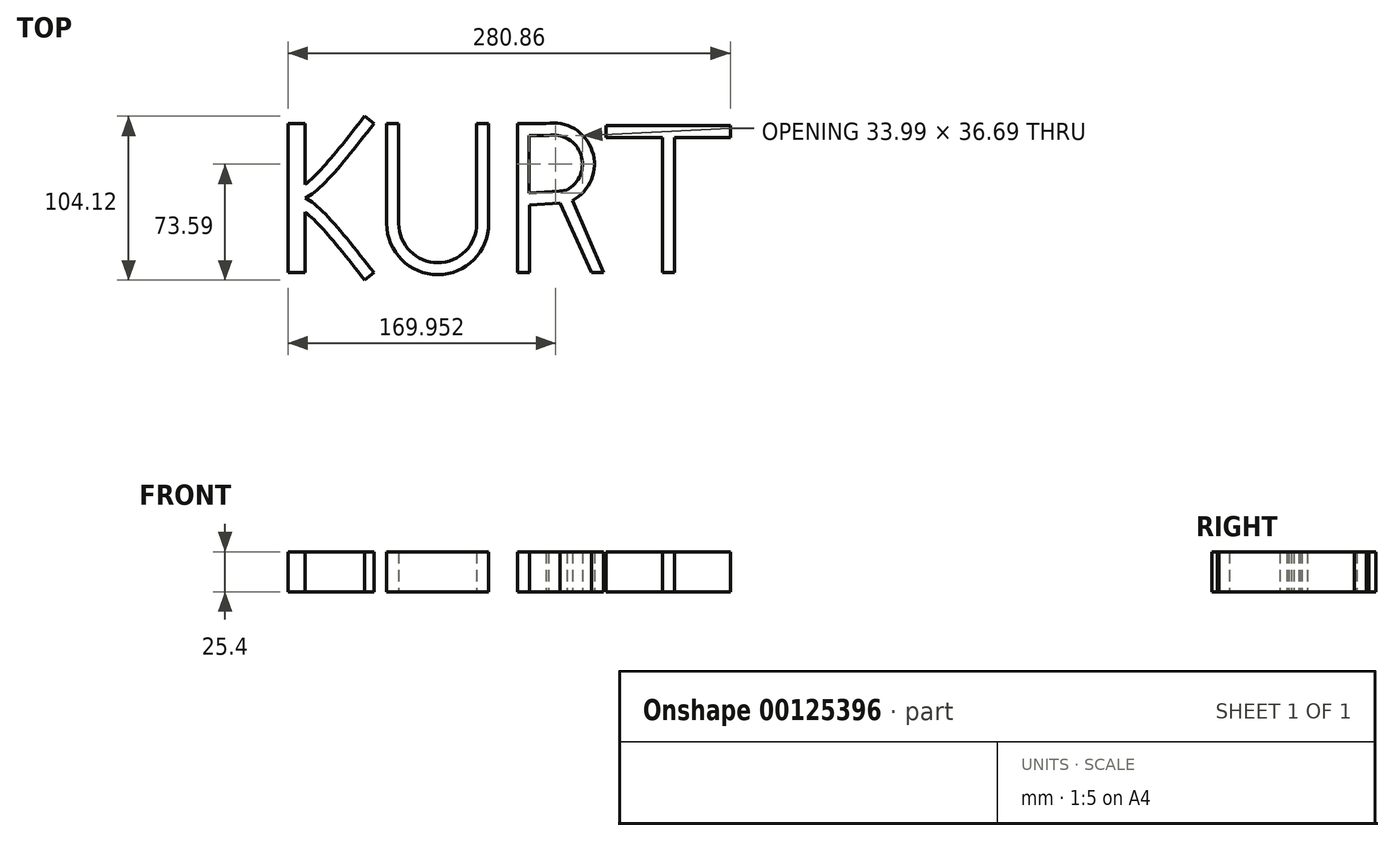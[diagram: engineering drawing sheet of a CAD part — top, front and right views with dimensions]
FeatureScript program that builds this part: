
annotation { "Feature Type Name" : "Feature", "Feature Type Description" : "" }
export const myFeature = defineFeature(function(context is Context, id is Id, definition is map)
    precondition{}
    {
        {
            var Q0;
            Q0=qCreatedBy(makeId("Top.planeOp"),FACE);
            var sketch = newSketch(context, id + "F0", { "sketchPlane" : qUnion([Q0])});
            skLineSegment(sketch, "E0.bottom", {"start": v(-95.51, 40.74) * mm, "end": v(-84.71, 40.74) * mm});
            skLineSegment(sketch, "E0.top", {"start": v(-95.51, -54.02) * mm, "end": v(-84.71, -54.02) * mm});
            skLineSegment(sketch, "E0.left", {"start": v(-95.51, 40.74) * mm, "end": v(-95.51, -54.02) * mm});
            skLineSegment(sketch, "E0.right", {"start": v(-84.71, 40.74) * mm, "end": v(-84.71, -54.02) * mm});
            skFitSpline(sketch, "E1", {"points": [v(-95.51, -6.64) * mm, v(-84.71, -6.64) * mm, v(-41.01, 40.74) * mm], "startDerivative": vector(33.65, -9.7) * mm, "endDerivative": vector(70.25, 90.47) * mm});
            skFitSpline(sketch, "E2", {"points": [v(-95.51, -6.64) * mm, v(-84.71, -6.64) * mm, v(-41.01, -54.02) * mm], "startDerivative": vector(33.65, 9.7) * mm, "endDerivative": vector(70.25, -90.47) * mm});
            skFitSpline(sketch, "E3.0", {"points": [v(-93.4, 0.68) * mm, v(-92.7, 0.48) * mm, v(-91.5, 0.14) * mm, v(-90.45, -0.06) * mm, v(-89.82, -0.1) * mm, v(-89.41, -0.1) * mm, v(-89.01, -0.06) * mm, v(-88.56, 0.04) * mm, v(-88.08, 0.2) * mm, v(-87.63, 0.4) * mm, v(-87.23, 0.6) * mm, v(-86.77, 0.84) * mm, v(-86.1, 1.25) * mm, v(-84.75, 2.14) * mm, v(-82.47, 3.92) * mm, v(-79.32, 6.78) * mm, v(-75.87, 10.27) * mm, v(-72.17, 14.3) * mm, v(-68.27, 18.78) * mm, v(-62.86, 25.27) * mm, v(-55.8, 34.13) * mm, v(-49.96, 41.65) * mm, v(-47.03, 45.42) * mm]});
            skFitSpline(sketch, "E4.0", {"points": [v(-93.4, -13.96) * mm, v(-92.7, -13.76) * mm, v(-91.5, -13.42) * mm, v(-90.45, -13.22) * mm, v(-89.82, -13.17) * mm, v(-89.41, -13.18) * mm, v(-89.01, -13.22) * mm, v(-88.56, -13.32) * mm, v(-88.08, -13.48) * mm, v(-87.63, -13.68) * mm, v(-87.23, -13.87) * mm, v(-86.77, -14.12) * mm, v(-86.1, -14.52) * mm, v(-84.75, -15.41) * mm, v(-82.47, -17.2) * mm, v(-79.32, -20.06) * mm, v(-75.87, -23.54) * mm, v(-72.17, -27.57) * mm, v(-68.27, -32.06) * mm, v(-62.86, -38.55) * mm, v(-55.8, -47.41) * mm, v(-49.96, -54.93) * mm, v(-47.03, -58.7) * mm]});
            skLineSegment(sketch, "E5", {"start": v(-47.03, 45.42) * mm, "end": v(-41.01, 40.74) * mm});
            skLineSegment(sketch, "E6", {"start": v(-47.03, -58.7) * mm, "end": v(-41.01, -54.02) * mm});
            skLineSegment(sketch, "E7", {"start": v(-25.26, 40.74) * mm, "end": v(-25.26, -22.76) * mm});
            skLineSegment(sketch, "E8", {"start": v(24.34, 40.74) * mm, "end": v(24.34, -22.76) * mm});
            skArc(sketch, "E9", {"start": v(-25.26, -22.76) * mm, "mid": v(-0.46, -47.55) * mm, "end": v(24.34, -22.76) * mm});
            skLineSegment(sketch, "E10.0", {"start": v(31.96, 40.74) * mm, "end": v(31.96, -22.76) * mm});
            skArc(sketch, "E10.1", {"start": v(-32.88, -22.76) * mm, "mid": v(-0.46, -55.17) * mm, "end": v(31.96, -22.76) * mm});
            skLineSegment(sketch, "E10.2", {"start": v(-32.88, 40.74) * mm, "end": v(-32.88, -22.76) * mm});
            skLineSegment(sketch, "E11", {"start": v(-32.88, 40.74) * mm, "end": v(-25.26, 40.74) * mm});
            skLineSegment(sketch, "E12", {"start": v(24.34, 40.74) * mm, "end": v(31.96, 40.74) * mm});
            skLineSegment(sketch, "E13", {"start": v(50.32, 40.74) * mm, "end": v(50.32, -54.02) * mm});
            skPoint(sketch, "E13.endSnap0", {"position": v(-90.11, -54.02) * mm});
            skLineSegment(sketch, "E14", {"start": v(50.32, -54.02) * mm, "end": v(57.93, -54.02) * mm});
            skLineSegment(sketch, "E15", {"start": v(57.93, -54.02) * mm, "end": v(57.93, -11.06) * mm});
            skLineSegment(sketch, "E16", {"start": v(50.32, 40.74) * mm, "end": v(68.49, 40.74) * mm});
            skArc(sketch, "E17", {"start": v(68.49, 40.74) * mm, "mid": v(97.68, 23.35) * mm, "end": v(85.06, -8.2) * mm});
            skLineSegment(sketch, "E18", {"start": v(85.06, -8.2) * mm, "end": v(104.82, -54.02) * mm});
            skLineSegment(sketch, "E19", {"start": v(104.82, -54.02) * mm, "end": v(97.2, -54.02) * mm});
            skLineSegment(sketch, "E20", {"start": v(97.2, -54.02) * mm, "end": v(77.33, -9.83) * mm});
            skLineSegment(sketch, "E21", {"start": v(57.93, -11.06) * mm, "end": v(77.33, -9.83) * mm});
            skArc(sketch, "E22.0", {"start": v(69.77, 33.23) * mm, "mid": v(90.46, 20.91) * mm, "end": v(81.52, -1.45) * mm});
            skLineSegment(sketch, "E23.0", {"start": v(57.45, -3.45) * mm, "end": v(76.84, -2.23) * mm});
            skLineSegment(sketch, "E24", {"start": v(76.84, -2.23) * mm, "end": v(81.52, -1.45) * mm});
            skLineSegment(sketch, "E25", {"start": v(57.45, -3.45) * mm, "end": v(57.45, 33.23) * mm});
            skLineSegment(sketch, "E26", {"start": v(57.45, 33.23) * mm, "end": v(69.77, 33.23) * mm});
            skLineSegment(sketch, "E27.bottom", {"start": v(106.54, 39.53) * mm, "end": v(185.35, 39.53) * mm});
            skLineSegment(sketch, "E27.top", {"start": v(106.54, 31.9) * mm, "end": v(185.35, 31.9) * mm});
            skLineSegment(sketch, "E27.left", {"start": v(106.54, 39.53) * mm, "end": v(106.54, 31.9) * mm});
            skLineSegment(sketch, "E27.right", {"start": v(185.35, 39.53) * mm, "end": v(185.35, 31.9) * mm});
            skPoint(sketch, "E28.endSnap0", {"position": v(101.01, -54.02) * mm});
            skLineSegment(sketch, "E29.bottom", {"start": v(145.95, 31.9) * mm, "end": v(142.14, 31.9) * mm});
            skLineSegment(sketch, "E29.top", {"start": v(145.95, -54.02) * mm, "end": v(142.14, -54.02) * mm});
            skLineSegment(sketch, "E29.right", {"start": v(142.14, 31.9) * mm, "end": v(142.14, -54.02) * mm});
            skLineSegment(sketch, "E30.MirrorCS", {"start": v(149.76, 31.9) * mm, "end": v(149.76, -54.02) * mm});
            skLineSegment(sketch, "E31.MirrorCS", {"start": v(145.95, -54.02) * mm, "end": v(149.76, -54.02) * mm});
            skPoint(sketch, "E28.end.orphan", {"position": v(145.95, -54.02) * mm});
            skSolve(sketch);
        }
        {
            var Q0;
            Q0 = qSketchRegion(id + "F0", true);
            extrude(context, id + "F1", {"entities" : qUnion([Q0]), "depth" : 25.4 * mm});
        }
    });
